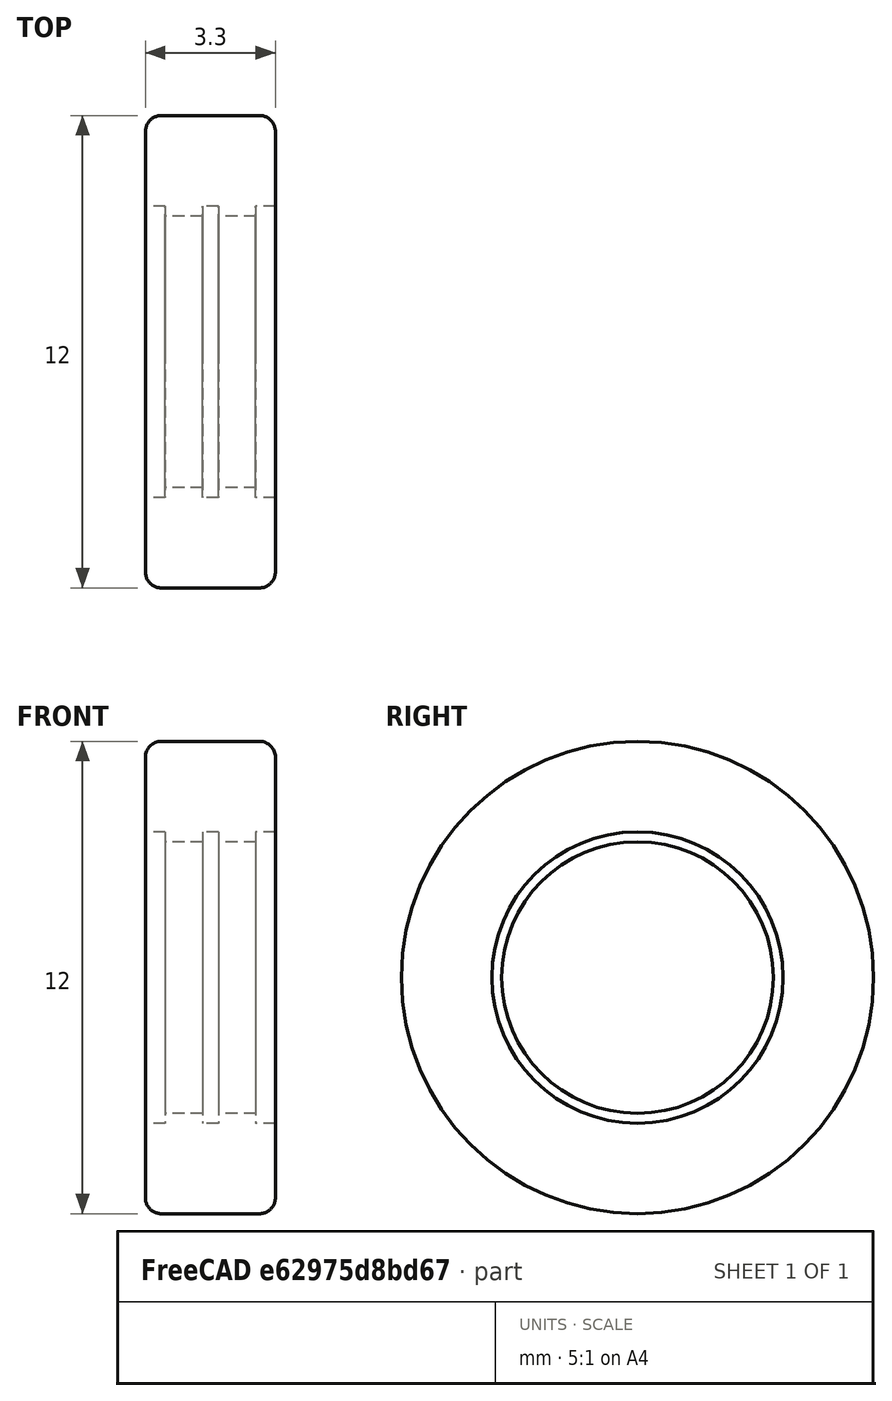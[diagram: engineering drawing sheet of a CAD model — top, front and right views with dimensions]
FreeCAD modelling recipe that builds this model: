
FCSTD DOCUMENT  (FreeCAD 0.16R6264 (Git))
Label: Pneu
License: All rights reserved
LicenseURL: http://en.wikipedia.org/wiki/All_rights_reserved
objects: Sketcher::SketchObject×1, PartDesign::Revolution×1
note: 3 computed .brp shape members not serialized (recipe doc carries the construction recipe); baked Part::Feature solids carry a one-line shape summary decoded from their .brp

FEATURE [Sketcher::SketchObject] Sketch
  Placement = pos=(0,0,0) rot=(1,0,0;1.5708rad)
  sketch-geometry (14):
    g0: LineSegment StartX=-1.65 StartY=3.7 StartZ=0 EndX=-1.65 EndY=5.6 EndZ=0
    g1: LineSegment StartX=-1.25 StartY=6 StartZ=0 EndX=1.25 EndY=6 EndZ=0
    g2: LineSegment StartX=1.65 StartY=5.6 StartZ=0 EndX=1.65 EndY=3.7 EndZ=0
    g3: LineSegment StartX=1.65 StartY=3.7 StartZ=0 EndX=1.15 EndY=3.7 EndZ=0
    g4: LineSegment StartX=1.15 StartY=3.7 StartZ=0 EndX=1.15 EndY=3.45 EndZ=0
    g5: LineSegment StartX=1.15 StartY=3.45 StartZ=0 EndX=0.2 EndY=3.45 EndZ=0
    g6: LineSegment StartX=0.2 StartY=3.45 StartZ=0 EndX=0.2 EndY=3.7 EndZ=0
    g7: LineSegment StartX=0.2 StartY=3.7 StartZ=0 EndX=-0.2 EndY=3.7 EndZ=0
    g8: LineSegment StartX=-0.2 StartY=3.7 StartZ=0 EndX=-0.2 EndY=3.45 EndZ=0
    g9: LineSegment StartX=-0.2 StartY=3.45 StartZ=0 EndX=-1.15 EndY=3.45 EndZ=0
    g10: LineSegment StartX=-1.15 StartY=3.45 StartZ=0 EndX=-1.15 EndY=3.7 EndZ=0
    g11: LineSegment StartX=-1.15 StartY=3.7 StartZ=0 EndX=-1.65 EndY=3.7 EndZ=0
    g12: ArcOfCircle CenterX=-1.25 CenterY=5.6 CenterZ=0 NormalX=0 NormalY=0 NormalZ=1 Radius=0.4 StartAngle=1.5708 EndAngle=3.14159
    g13: ArcOfCircle CenterX=1.25 CenterY=5.6 CenterZ=0 NormalX=0 NormalY=0 NormalZ=1 Radius=0.4 StartAngle=0 EndAngle=1.5708
  constraints (40):
    c: Vertical(g0)
    c: Horizontal(g1)
    c: Vertical(g2)
    c: Coincident(g2,g3)
    c: Horizontal(g3)
    c: Coincident(g3,g4)
    c: Coincident(g4,g5)
    c: Coincident(g5,g6)
    c: Vertical(g6)
    c: Coincident(g6,g7)
    c: Horizontal(g7)
    c: Coincident(g7,g8)
    c: Vertical(g8)
    c: Coincident(g8,g9)
    c: Horizontal(g9)
    c: Coincident(g9,g10)
    c: Vertical(g10)
    c: Coincident(g10,g11)
    c: Horizontal(g11)
    c: Vertical(g4)
    c: Horizontal(g5)
    c: Coincident(g0,g11)
    c: Tangent(g0,g12) = 1.5708
    c: Tangent(g1,g12) = 1.5708
    c: Tangent(g1,g13) = 1.5708
    c: Tangent(g2,g13) = 1.5708
    c: Radius(g12) = 0.4
    c: Equal(g12,g13)
    c: DistanceX(g2,g0) = -3.3
    c: DistanceY(g1) = 6
    c: DistanceY(g4) = 3.45
    c: Equal(g6,g8)
    c: DistanceY(g2) = 3.7
    c: Equal(g4,g10)
    c: Equal(g6,g4)
    c: Equal(g11,g3)
    c: DistanceX(g4,g2) = 0.5
    c: DistanceX(g7) = -0.4
    c: DistanceX(g2) = 1.65
    c: Equal(g5,g9)
FEATURE [PartDesign::Revolution] Revolution
  Angle = 360
  Axis = (1,0,0)
  Base = (0,0,0)
  Placement = pos=(0,0,0) rot=(1,0,0;1.5708rad)
  ReferenceAxis = -> Sketch [H_Axis]
  Sketch = -> Sketch
